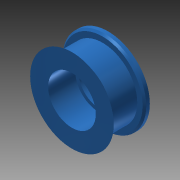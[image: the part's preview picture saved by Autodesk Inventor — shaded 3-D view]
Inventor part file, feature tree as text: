
AUTODESK INVENTOR PART (.ipt)
format: ipt  version: 2013 SP2 (Build 170200200, 200)  size: 117,248 bytes
history: native  units: mm
features: revolve x1, sketch x1
ambient origin geometry x8: Origin, YZ Plane, XZ Plane, XY Plane, X Axis, Y Axis, Z Axis, Center Point
bodies: Solid1 (feature_tree)
feature tree (2):
  revolve  "Revolution1"  [1 undecoded]
  sketch  "Sketch1"  dims[d6=10.0mm d7=6.6mm d10=90.0deg d14=5.0mm d17=7.0mm d18=1.5mm d19=135.0deg d20=2.0mm d21=1.0mm d22=2.5mm]
note: 1 required parameter value undecoded (feature->parameter linkage not recoverable at this tier; creation-order binding heuristic only, values carry confidence <= 0.55)
